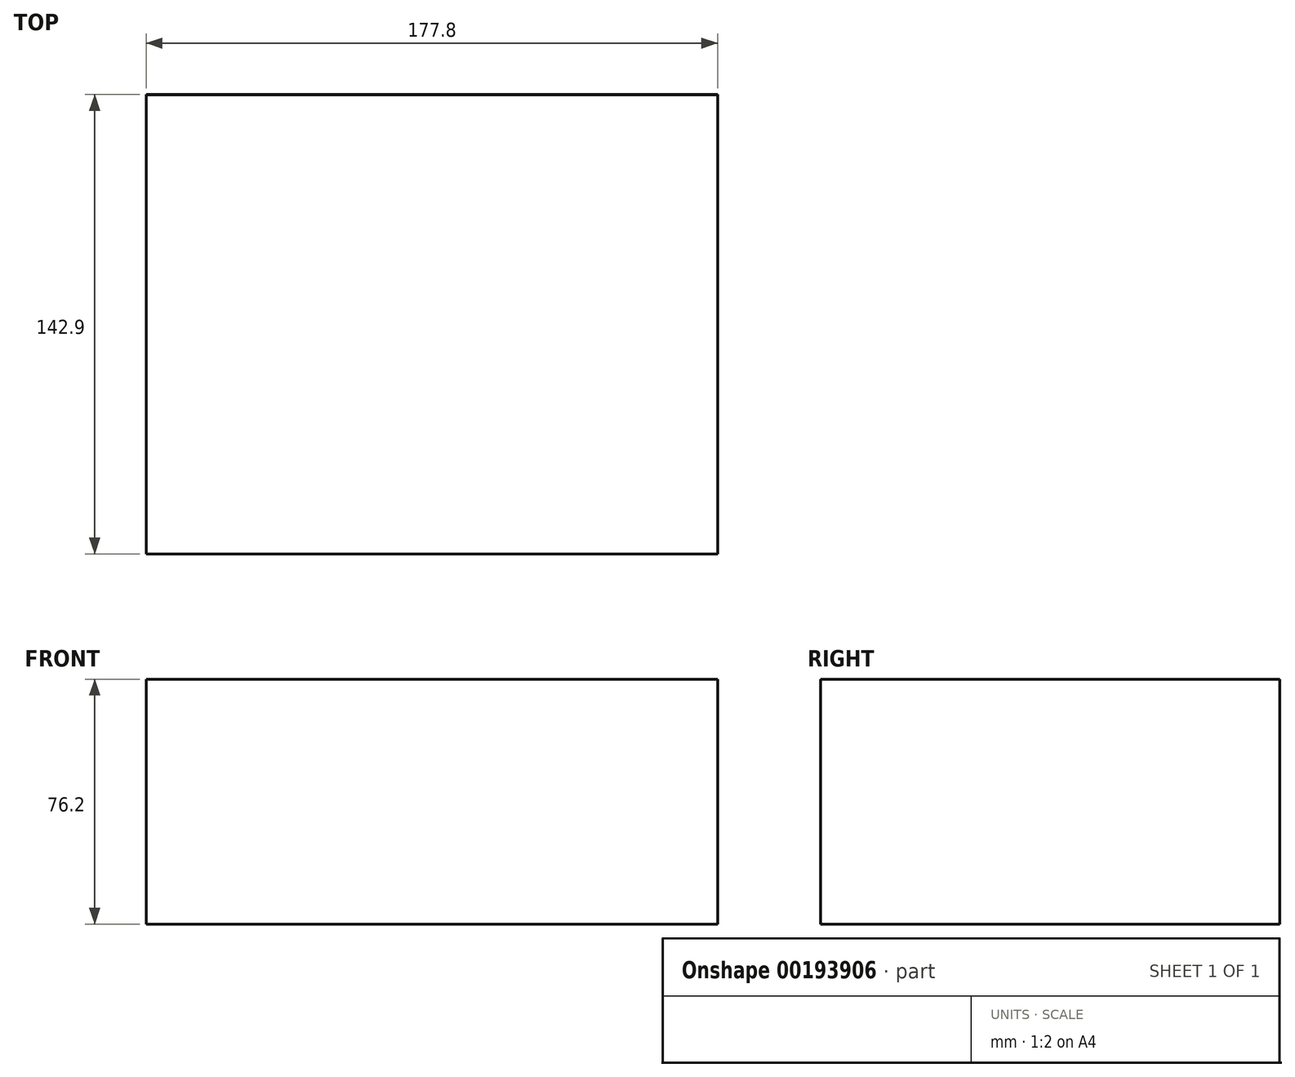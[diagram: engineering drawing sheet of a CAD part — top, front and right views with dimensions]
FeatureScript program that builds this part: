
annotation { "Feature Type Name" : "Feature", "Feature Type Description" : "" }
export const myFeature = defineFeature(function(context is Context, id is Id, definition is map)
    precondition{}
    {
        {
            var Q0;
            Q0=qCreatedBy(makeId("Top.planeOp"),FACE);
            var sketch = newSketch(context, id + "F0", { "sketchPlane" : qUnion([Q0])});
            skLineSegment(sketch, "E0.bottom", {"start": v(-95.3, 56.61) * mm, "end": v(82.5, 56.61) * mm});
            skLineSegment(sketch, "E0.top", {"start": v(-95.3, -86.26) * mm, "end": v(82.5, -86.26) * mm});
            skLineSegment(sketch, "E0.left", {"start": v(-95.3, 56.61) * mm, "end": v(-95.3, -86.26) * mm});
            skLineSegment(sketch, "E0.right", {"start": v(82.5, 56.61) * mm, "end": v(82.5, -86.26) * mm});
            skSolve(sketch);
        }
        {
            var Q0;
            Q0=makeQuery(id+"F0.imprint","IMPRINT",FACE,{"disambiguationData":[TD([[makeQuery(id+"F0.imprint","IMPRINT",EDGE,{"derivedFrom":sQuery(id+"F0.wireOp",EDGE,"E0.bottom")}),-1.0]])]});
            extrude(context, id + "F1", {"entities" : qUnion([Q0]), "depth" : 76.2 * mm});
        }
        {
            var Q0;
            Q0=makeQuery(id+"F1.opExtrude","SWEPT_FACE",FACE,{"disambiguationData":[OSD([sQuery(id+"F0.wireOp",EDGE,"E0.bottom")])]});
            extrude(context, id + "F2", {"entities" : qUnion([Q0]), "depth" : 5 / 203.2 * mm});
        }
    });
